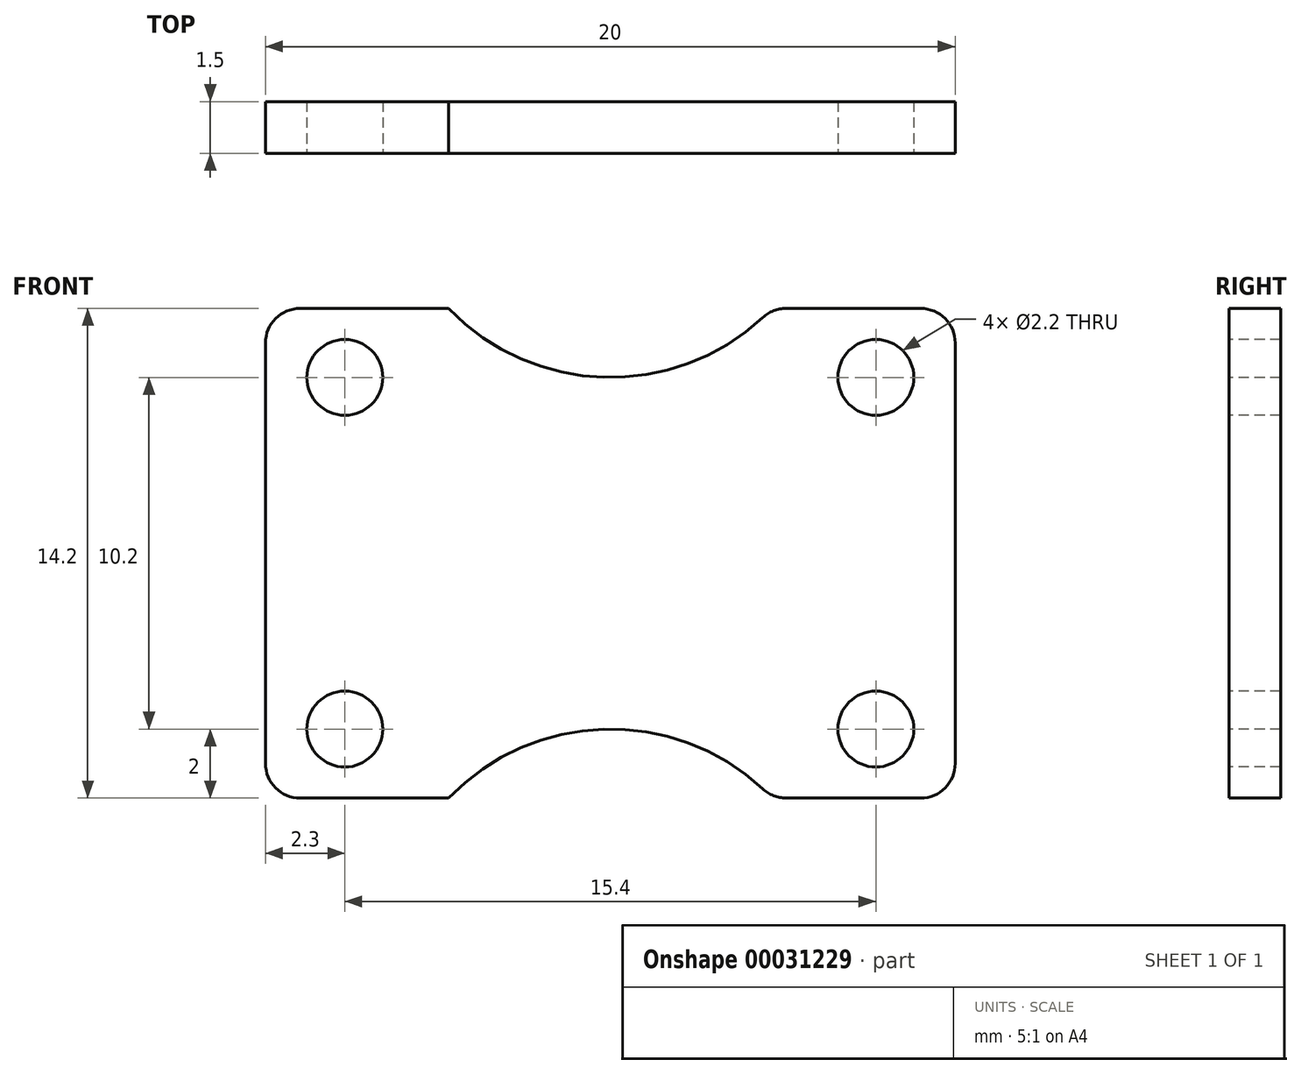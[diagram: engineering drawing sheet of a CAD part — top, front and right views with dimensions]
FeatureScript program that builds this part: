
annotation { "Feature Type Name" : "Feature", "Feature Type Description" : "" }
export const myFeature = defineFeature(function(context is Context, id is Id, definition is map)
    precondition{}
    {
        {
            var Q0;
            Q0=qCreatedBy(makeId("Front.planeOp"),FACE);
            var sketch = newSketch(context, id + "F0", { "sketchPlane" : qUnion([Q0])});
            skLineSegment(sketch, "E0.bottom", {"start": v(0, 0) * mm, "end": v(20, 0) * mm});
            skLineSegment(sketch, "E0.top", {"start": v(0, 14.2) * mm, "end": v(20, 14.2) * mm});
            skLineSegment(sketch, "E0.left", {"start": v(0, 0) * mm, "end": v(0, 14.2) * mm});
            skLineSegment(sketch, "E0.right", {"start": v(20, 0) * mm, "end": v(20, 14.2) * mm});
            skSolve(sketch);
        }
        {
            var Q0;
            Q0=qSketchRegion(id+"F0",true);
            extrude(context, id + "F1", {"entities" : qUnion([Q0]), "depth" : 1.5 * mm});
        }
        {
            var Q0;
            Q0=makeQuery(id+"F1.opExtrude","CAP_FACE",FACE,{"disambiguationData":[OSD([sQuery(id+"F0.wireOp",EDGE,"E0.bottom"),sQuery(id+"F0.wireOp",EDGE,"E0.top"),sQuery(id+"F0.wireOp",EDGE,"E0.left"),sQuery(id+"F0.wireOp",EDGE,"E0.right")])],"isStart":false});
            var sketch = newSketch(context, id + "F2", { "sketchPlane" : qUnion([Q0])});
            skLineSegment(sketch, "E1", {"start": v(0, 7.1) * mm, "end": v(20, 7.1) * mm, "construction": true});
            skLineSegment(sketch, "E2", {"start": v(10, 14.2) * mm, "end": v(10, 0) * mm, "construction": true});
            skPoint(sketch, "E3", {"position": v(10, 7.1) * mm});
            skCircle(sketch, "E4", {"center": v(2.3, 12.2) * mm, "radius": 1.1 * mm});
            skCircle(sketch, "E5.MirrorC", {"center": v(17.7, 12.2) * mm, "radius": 1.1 * mm});
            skCircle(sketch, "E6.MirrorC", {"center": v(2.3, 2) * mm, "radius": 1.1 * mm});
            skCircle(sketch, "E7.MirrorC", {"center": v(17.7, 2) * mm, "radius": 1.1 * mm});
            skLineSegment(sketch, "E8", {"start": v(0, 18.7) * mm, "end": v(20.46, 18.7) * mm, "construction": true});
            skPoint(sketch, "E9", {"position": v(10, 18.7) * mm});
            skArc(sketch, "E10", {"start": v(5.3, 14.2) * mm, "mid": v(10, 12.2) * mm, "end": v(14.7, 14.2) * mm});
            skLineSegment(sketch, "E11", {"start": v(5.3, 14.2) * mm, "end": v(14.7, 14.2) * mm});
            skArc(sketch, "E12.MirrorCS", {"start": v(5.3, 0) * mm, "mid": v(10, 2) * mm, "end": v(14.7, 0) * mm});
            skLineSegment(sketch, "E13.MirrorCS", {"start": v(5.3, 0) * mm, "end": v(14.7, 0) * mm});
            skCircle(sketch, "E14", {"center": v(10, 37.1) * mm, "radius": 5 * mm, "construction": true});
            skCircle(sketch, "E15.MirrorC", {"center": v(10, -22.9) * mm, "radius": 5 * mm, "construction": true});
            skSolve(sketch);
        }
        {
            var Q0;
            Q0=qSketchRegion(id+"F2",true);
            extrude(context, id + "F3", {"entities" : qUnion([Q0]), "operationType" : NewBodyOperationType.REMOVE, "endBound" : BoundingType.UP_TO_NEXT, "oppositeDirection" : true, "depth" : 25 * mm});
        }
        {
            var Q0;
            Q0=makeQuery(id+"F1.opExtrude","SWEPT_EDGE",EDGE,{"disambiguationData":[OSD([sQuery(id+"F0.wireOp",EDGE,"E0.top"),sQuery(id+"F0.wireOp",EDGE,"E0.right")])]});
            var Q1;
            Q1=makeQuery(id+"F1.opExtrude","SWEPT_EDGE",EDGE,{"disambiguationData":[OSD([sQuery(id+"F0.wireOp",EDGE,"E0.bottom"),sQuery(id+"F0.wireOp",EDGE,"E0.right")])]});
            var Q2;
            Q2=makeQuery(id+"F1.opExtrude","SWEPT_EDGE",EDGE,{"disambiguationData":[OSD([sQuery(id+"F0.wireOp",EDGE,"E0.top"),sQuery(id+"F0.wireOp",EDGE,"E0.left")])]});
            var Q3;
            Q3=makeQuery(id+"F1.opExtrude","SWEPT_EDGE",EDGE,{"disambiguationData":[OSD([sQuery(id+"F0.wireOp",EDGE,"E0.bottom"),sQuery(id+"F0.wireOp",EDGE,"E0.left")])]});
            var Q4;
            {var subQ0=sQuery(id+"F0.wireOp",EDGE,"E0.top");var subQ1=sQuery(id+"F2.wireOp",EDGE,"E10");var subQ2=sQuery(id+"F2.wireOp",EDGE,"E11");Q4=makeQuery(id+"F3.boolean.opBoolean","COPY",EDGE,{"derivedFrom":makeQuery(id+"F3.opExtrude","SWEPT_EDGE",EDGE,{"disambiguationData":[OSD([subQ0,subQ1,subQ2]),TDD([makeQuery(id+"F2.imprint","INTERSECT",VERTEX,{"disambiguationData":[OD(0.0)],"derivedFrom":[makeQuery(id+"F1.opExtrude","CAP_EDGE",EDGE,{"disambiguationData":[OSD([subQ0])],"isStart":false}),subQ1,subQ2]})])]})});}
            var Q5;
            {var subQ0=sQuery(id+"F0.wireOp",EDGE,"E0.top");var subQ1=sQuery(id+"F2.wireOp",EDGE,"E10");var subQ2=sQuery(id+"F2.wireOp",EDGE,"E11");Q5=makeQuery(id+"F3.boolean.opBoolean","COPY",EDGE,{"derivedFrom":makeQuery(id+"F3.opExtrude","SWEPT_EDGE",EDGE,{"disambiguationData":[OSD([subQ0,subQ1,subQ2]),TDD([makeQuery(id+"F2.imprint","INTERSECT",VERTEX,{"disambiguationData":[OD(1.0)],"derivedFrom":[makeQuery(id+"F1.opExtrude","CAP_EDGE",EDGE,{"disambiguationData":[OSD([subQ0])],"isStart":false}),subQ1,subQ2]})])]})});}
            var Q6;
            {var subQ0=sQuery(id+"F0.wireOp",EDGE,"E0.bottom");var subQ1=sQuery(id+"F2.wireOp",EDGE,"E12.MirrorCS");var subQ2=sQuery(id+"F2.wireOp",EDGE,"E13.MirrorCS");Q6=makeQuery(id+"F3.boolean.opBoolean","COPY",EDGE,{"derivedFrom":makeQuery(id+"F3.opExtrude","SWEPT_EDGE",EDGE,{"disambiguationData":[OSD([subQ0,subQ1,subQ2]),TDD([makeQuery(id+"F2.imprint","INTERSECT",VERTEX,{"disambiguationData":[OD(0.0)],"derivedFrom":[makeQuery(id+"F1.opExtrude","CAP_EDGE",EDGE,{"disambiguationData":[OSD([subQ0])],"isStart":false}),subQ1,subQ2]})])]})});}
            var Q7;
            {var subQ0=sQuery(id+"F0.wireOp",EDGE,"E0.bottom");var subQ1=sQuery(id+"F2.wireOp",EDGE,"E12.MirrorCS");var subQ2=sQuery(id+"F2.wireOp",EDGE,"E13.MirrorCS");Q7=makeQuery(id+"F3.boolean.opBoolean","COPY",EDGE,{"derivedFrom":makeQuery(id+"F3.opExtrude","SWEPT_EDGE",EDGE,{"disambiguationData":[OSD([subQ0,subQ1,subQ2]),TDD([makeQuery(id+"F2.imprint","INTERSECT",VERTEX,{"disambiguationData":[OD(1.0)],"derivedFrom":[makeQuery(id+"F1.opExtrude","CAP_EDGE",EDGE,{"disambiguationData":[OSD([subQ0])],"isStart":false}),subQ1,subQ2]})])]})});}
            fillet(context, id + "F4", {"entities" : qUnion([Q0, Q1, Q2, Q3, Q4, Q5, Q6, Q7]), "radius" : 1 * mm, "tangentPropagation" : true, "allowEdgeOverflow" : false});
        }
    });
